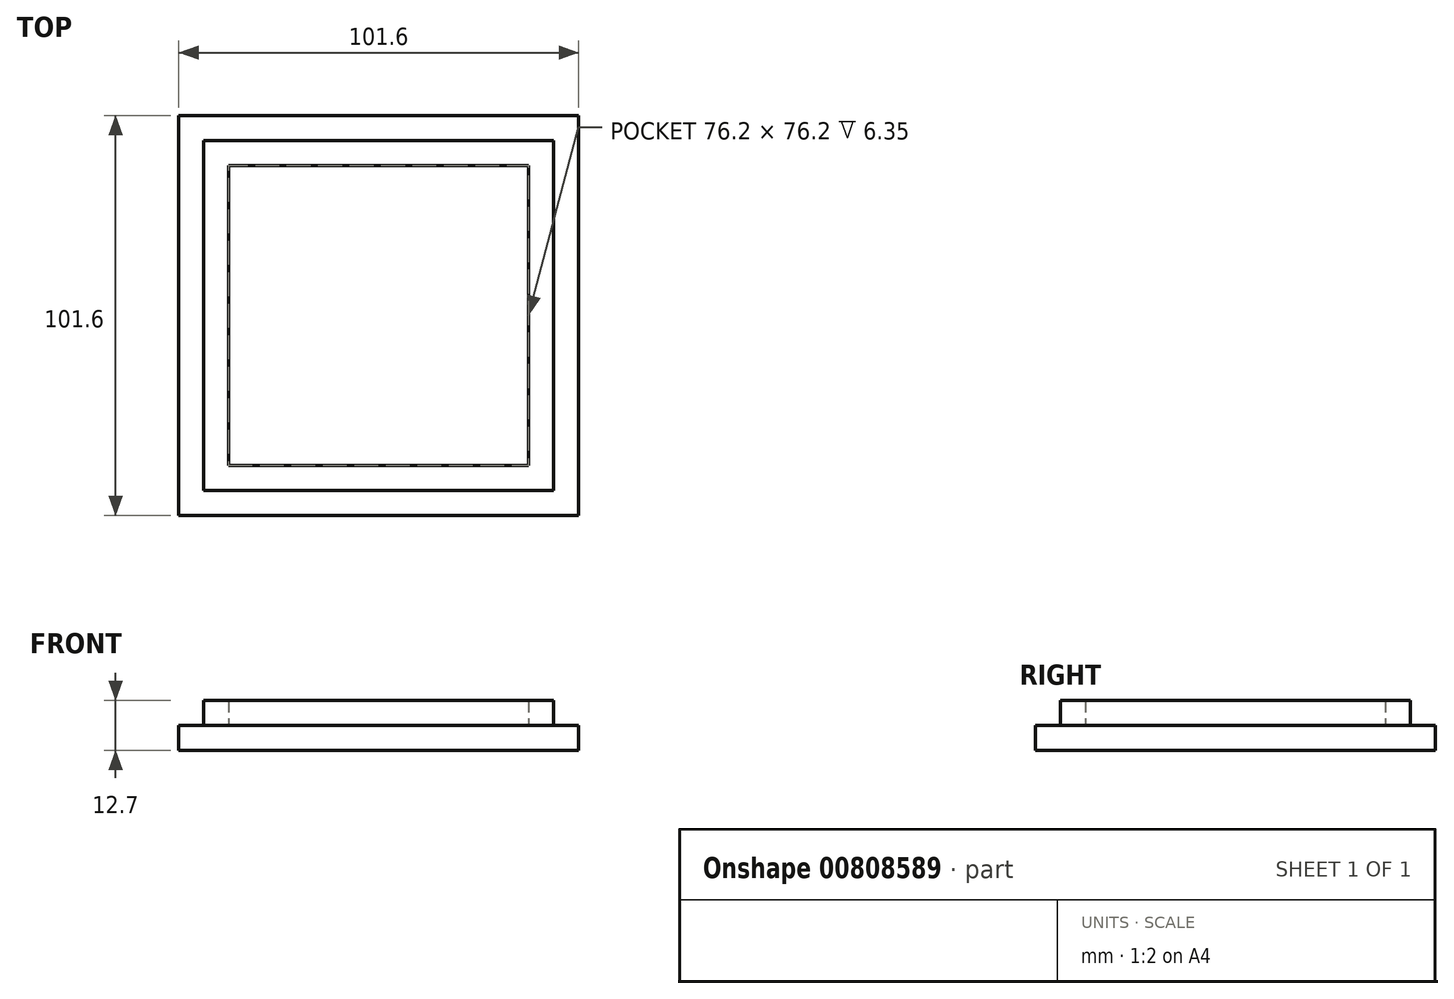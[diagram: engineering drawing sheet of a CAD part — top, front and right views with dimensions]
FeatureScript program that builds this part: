
annotation { "Feature Type Name" : "Feature", "Feature Type Description" : "" }
export const myFeature = defineFeature(function(context is Context, id is Id, definition is map)
    precondition{}
    {
        {
            var Q0;
            Q0=qCreatedBy(makeId("Top.planeOp"),FACE);
            var sketch = newSketch(context, id + "F0", { "sketchPlane" : qUnion([Q0])});
            skLineSegment(sketch, "E0.bottom", {"start": v(50.8, 50.8) * mm, "end": v(-50.8, 50.8) * mm});
            skLineSegment(sketch, "E0.top", {"start": v(50.8, -50.8) * mm, "end": v(-50.8, -50.8) * mm});
            skLineSegment(sketch, "E0.left", {"start": v(50.8, 50.8) * mm, "end": v(50.8, -50.8) * mm});
            skLineSegment(sketch, "E0.right", {"start": v(-50.8, 50.8) * mm, "end": v(-50.8, -50.8) * mm});
            skPoint(sketch, "E0.middle", {"position": v(0, 0) * mm});
            skSolve(sketch);
        }
        {
            var Q0;
            Q0 = qSketchRegion(id + "F0", true);
            extrude(context, id + "F1", {"entities" : qUnion([Q0]), "depth" : 6.35 * mm, "offsetDistance" : 25.4 * mm});
        }
        {
            var Q0;
            Q0=makeQuery(id+"F1.opExtrude","CAP_FACE",FACE,{"disambiguationData":[OSD([sQuery(id+"F0.wireOp",EDGE,"E0.bottom"),sQuery(id+"F0.wireOp",EDGE,"E0.top"),sQuery(id+"F0.wireOp",EDGE,"E0.left"),sQuery(id+"F0.wireOp",EDGE,"E0.right")])],"isStart":false});
            var sketch = newSketch(context, id + "F2", { "sketchPlane" : qUnion([Q0])});
            skLineSegment(sketch, "E1.bottom", {"start": v(44.45, 44.45) * mm, "end": v(-44.45, 44.45) * mm});
            skLineSegment(sketch, "E1.top", {"start": v(44.45, -44.45) * mm, "end": v(-44.45, -44.45) * mm});
            skLineSegment(sketch, "E1.left", {"start": v(44.45, 44.45) * mm, "end": v(44.45, -44.45) * mm});
            skLineSegment(sketch, "E1.right", {"start": v(-44.45, 44.45) * mm, "end": v(-44.45, -44.45) * mm});
            skPoint(sketch, "E1.middle", {"position": v(0, 0) * mm});
            skLineSegment(sketch, "E2.bottom", {"start": v(38.1, 38.1) * mm, "end": v(-38.1, 38.1) * mm});
            skLineSegment(sketch, "E2.top", {"start": v(38.1, -38.1) * mm, "end": v(-38.1, -38.1) * mm});
            skLineSegment(sketch, "E2.left", {"start": v(38.1, 38.1) * mm, "end": v(38.1, -38.1) * mm});
            skLineSegment(sketch, "E2.right", {"start": v(-38.1, 38.1) * mm, "end": v(-38.1, -38.1) * mm});
            skSolve(sketch);
        }
        {
            var Q0;
            Q0=makeQuery(id+"F2.imprint","IMPRINT",FACE,{"disambiguationData":[TD([[makeQuery(id+"F2.imprint","IMPRINT",EDGE,{"derivedFrom":sQuery(id+"F2.wireOp",EDGE,"E1.bottom")}),1.0]])]});
            extrude(context, id + "F3", {"entities" : qUnion([Q0]), "operationType" : NewBodyOperationType.ADD, "depth" : 6.35 * mm, "offsetDistance" : 25.4 * mm});
        }
    });
